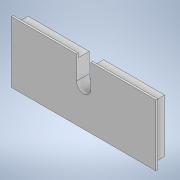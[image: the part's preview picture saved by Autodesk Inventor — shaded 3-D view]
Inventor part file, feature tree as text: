
AUTODESK INVENTOR PART (.ipt)
format: ipt  version: 2021 (Build 250183000, 183)  size: 274,432 bytes
history: native  units: in
note: dims shown in document units (in); Inventor stores cm internally (conversion verified against a paired STEP export)
features: extrude x3, sketch x3, projected_geometry x2, fillet x1
ambient origin geometry x8: Origin, YZ Plane, XZ Plane, XY Plane, X Axis, Y Axis, Z Axis, Center Point
bodies: Solid1 (feature_tree)
feature tree (9):
  extrude  "Extrusion1"  Depth=0.5807in
  extrude  "Extrusion2"  Depth=1.5748in
  extrude  "Extrusion3"  Depth=0.0197in TaperAngle=0.0deg
  fillet  "Fillet1"  Radius=0.1575in
  sketch  "Sketch1"  dims[d0=1.4862in d1=0.5807in]
  sketch  "Sketch2"  dims[d2=0.1181in d3=0.0in d4=1.5748in]
  projected_geometry  "Projected Loop1"
  sketch  "Sketch3"  dims[d5=0.6693in d6=0.0197in d7=0.0in d8=0.1575in d9=0.0in d10=0.0in d11=0.0787in]
  projected_geometry  "Projected Loop2"
